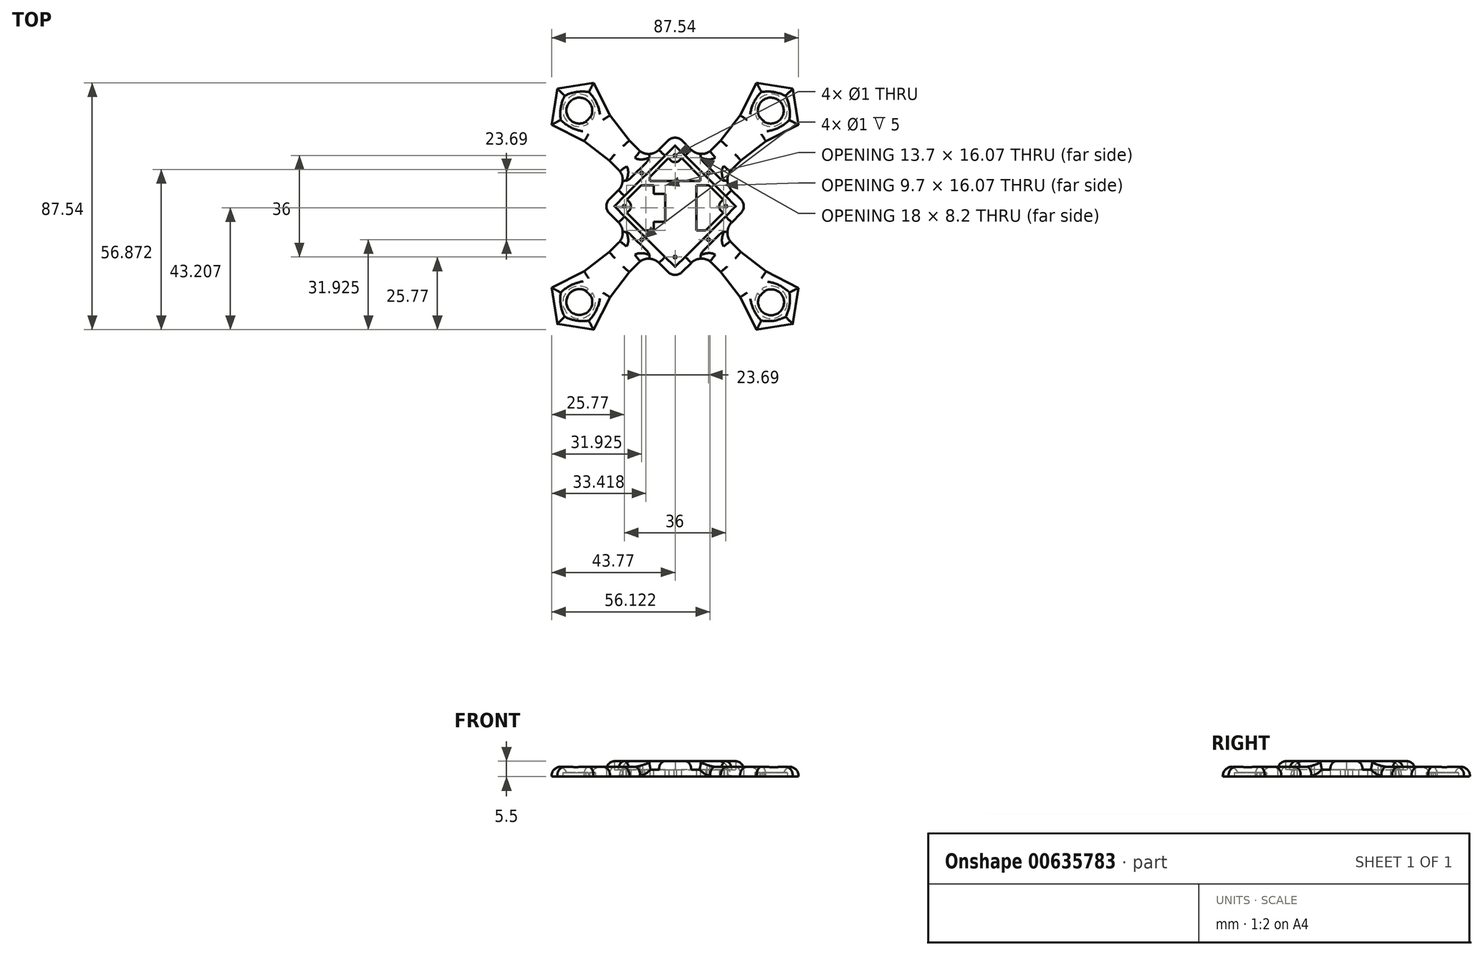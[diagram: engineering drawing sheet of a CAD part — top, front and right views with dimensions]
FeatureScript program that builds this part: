
annotation { "Feature Type Name" : "Feature", "Feature Type Description" : "" }
export const myFeature = defineFeature(function(context is Context, id is Id, definition is map)
    precondition{}
    {
        {
            var Q0;
            Q0=qCreatedBy(makeId("Top.planeOp"),FACE);
            var sketch = newSketch(context, id + "F0", { "sketchPlane" : qUnion([Q0])});
            skCircle(sketch, "E0", {"center": v(0, 18) * mm, "radius": 0.5 * mm});
            skCircle(sketch, "E1.1.0", {"center": v(-18, 0) * mm, "radius": 0.5 * mm});
            skCircle(sketch, "E1.2.0", {"center": v(0, -18) * mm, "radius": 0.5 * mm});
            skCircle(sketch, "E1.3.0", {"center": v(18, 0) * mm, "radius": 0.5 * mm});
            skPoint(sketch, "E1.center", {"position": v(0, 0) * mm});
            skLineSegment(sketch, "E2.0", {"start": v(-9, 10.41) * mm, "end": v(-9, 9) * mm});
            skLineSegment(sketch, "E3.0", {"start": v(9, 10.41) * mm, "end": v(9, 9) * mm});
            skLineSegment(sketch, "E4.0", {"start": v(-9, 9) * mm, "end": v(9, 9) * mm});
            skLineSegment(sketch, "E5.0", {"start": v(-21.54, 0) * mm, "end": v(0, -21.54) * mm});
            skLineSegment(sketch, "E5.1", {"start": v(-21.54, 0) * mm, "end": v(0, 21.54) * mm});
            skLineSegment(sketch, "E5.2", {"start": v(21.54, 0) * mm, "end": v(0, 21.54) * mm});
            skLineSegment(sketch, "E5.3", {"start": v(0, -21.54) * mm, "end": v(21.54, 0) * mm});
            skArc(sketch, "E6.0", {"start": v(-2.21, 17.2) * mm, "mid": v(0, 15.65) * mm, "end": v(2.21, 17.2) * mm});
            skArc(sketch, "E7.1.0", {"start": v(-17.2, -2.21) * mm, "mid": v(-15.65, 0) * mm, "end": v(-17.2, 2.21) * mm});
            skArc(sketch, "E7.3.0", {"start": v(17.2, 2.21) * mm, "mid": v(15.65, 0) * mm, "end": v(17.2, -2.21) * mm});
            skLineSegment(sketch, "E8.0", {"start": v(10.82, -8.6) * mm, "end": v(17.2, -2.21) * mm});
            skLineSegment(sketch, "E8.3", {"start": v(17.2, 2.21) * mm, "end": v(11.94, 7.47) * mm});
            skLineSegment(sketch, "E9.trimOffspring", {"start": v(-9, 10.41) * mm, "end": v(-2.21, 17.2) * mm});
            skLineSegment(sketch, "E10.trimOffspring", {"start": v(9, 10.41) * mm, "end": v(2.21, 17.2) * mm});
            skLineSegment(sketch, "E11.0", {"start": v(7.5, 7.47) * mm, "end": v(7.5, -8.6) * mm});
            skLineSegment(sketch, "E12", {"start": v(11.94, 7.47) * mm, "end": v(7.5, 7.47) * mm});
            skLineSegment(sketch, "E13", {"start": v(7.5, -8.6) * mm, "end": v(10.82, -8.6) * mm});
            skLineSegment(sketch, "E14.MirrorCS", {"start": v(-7.5, -8.6) * mm, "end": v(-10.82, -8.6) * mm});
            skLineSegment(sketch, "E15.MirrorCS", {"start": v(-7.5, 7.47) * mm, "end": v(-7.5, -8.6) * mm});
            skLineSegment(sketch, "E16.MirrorCS", {"start": v(-11.94, 7.47) * mm, "end": v(-7.5, 7.47) * mm});
            skLineSegment(sketch, "E17.MirrorCS", {"start": v(-10.82, -8.6) * mm, "end": v(-17.2, -2.21) * mm});
            skLineSegment(sketch, "E18.MirrorCS", {"start": v(21.54, 0) * mm, "end": v(0, -21.54) * mm});
            skLineSegment(sketch, "E19", {"start": v(-11.94, 7.47) * mm, "end": v(-17.2, 2.21) * mm});
            skSolve(sketch);
        }
        {
            var Q0;
            Q0 = qSketchRegion(id + "F0", true);
            extrude(context, id + "F1", {"entities" : qUnion([Q0]), "depth" : 2.5 * mm, "offsetDistance" : 25 * mm});
        }
        {
            var Q0;
            Q0=makeQuery(id+"F1.opExtrude","CAP_FACE",FACE,{"disambiguationData":[OSD([sQuery(id+"F0.wireOp",EDGE,"E0"),sQuery(id+"F0.wireOp",EDGE,"E1.1.0"),sQuery(id+"F0.wireOp",EDGE,"E1.2.0"),sQuery(id+"F0.wireOp",EDGE,"E1.3.0"),sQuery(id+"F0.wireOp",EDGE,"E2.0"),sQuery(id+"F0.wireOp",EDGE,"E3.0"),sQuery(id+"F0.wireOp",EDGE,"E4.0"),sQuery(id+"F0.wireOp",EDGE,"E5.0"),sQuery(id+"F0.wireOp",EDGE,"E5.1"),sQuery(id+"F0.wireOp",EDGE,"E5.2"),sQuery(id+"F0.wireOp",EDGE,"E6.0"),sQuery(id+"F0.wireOp",EDGE,"E7.1.0"),sQuery(id+"F0.wireOp",EDGE,"E7.3.0"),sQuery(id+"F0.wireOp",EDGE,"E8.0"),sQuery(id+"F0.wireOp",EDGE,"E8.3"),sQuery(id+"F0.wireOp",EDGE,"E9.trimOffspring"),sQuery(id+"F0.wireOp",EDGE,"E10.trimOffspring"),sQuery(id+"F0.wireOp",EDGE,"E11.0"),sQuery(id+"F0.wireOp",EDGE,"E12"),sQuery(id+"F0.wireOp",EDGE,"E13"),sQuery(id+"F0.wireOp",EDGE,"E14.MirrorCS"),sQuery(id+"F0.wireOp",EDGE,"E15.MirrorCS"),sQuery(id+"F0.wireOp",EDGE,"E16.MirrorCS"),sQuery(id+"F0.wireOp",EDGE,"E17.MirrorCS"),sQuery(id+"F0.wireOp",EDGE,"E18.MirrorCS"),sQuery(id+"F0.wireOp",EDGE,"E19")])],"isStart":false});
            var sketch = newSketch(context, id + "F2", { "sketchPlane" : qUnion([Q0])});
            skLineSegment(sketch, "E20", {"start": v(21.54, 0) * mm, "end": v(0, -21.54) * mm});
            skLineSegment(sketch, "E21", {"start": v(0, -21.54) * mm, "end": v(-21.54, 0) * mm});
            skLineSegment(sketch, "E22", {"start": v(-21.54, 0) * mm, "end": v(0, 21.54) * mm});
            skLineSegment(sketch, "E23", {"start": v(0, 21.54) * mm, "end": v(21.54, 0) * mm});
            skLineSegment(sketch, "E24.0", {"start": v(0, -25.78) * mm, "end": v(-25.78, 0) * mm});
            skLineSegment(sketch, "E24.1", {"start": v(25.78, 0) * mm, "end": v(0, -25.78) * mm});
            skLineSegment(sketch, "E24.2", {"start": v(0, 25.78) * mm, "end": v(25.78, 0) * mm});
            skLineSegment(sketch, "E24.3", {"start": v(-25.78, 0) * mm, "end": v(0, 25.78) * mm});
            skSolve(sketch);
        }
        {
            var Q0;
            Q0 = qSketchRegion(id + "F2", true);
            var Q1;
            Q1=makeQuery(id+"F1.opExtrude","CAP_FACE",FACE,{"disambiguationData":[OSD([sQuery(id+"F0.wireOp",EDGE,"E0"),sQuery(id+"F0.wireOp",EDGE,"E1.1.0"),sQuery(id+"F0.wireOp",EDGE,"E1.2.0"),sQuery(id+"F0.wireOp",EDGE,"E1.3.0"),sQuery(id+"F0.wireOp",EDGE,"E2.0"),sQuery(id+"F0.wireOp",EDGE,"E3.0"),sQuery(id+"F0.wireOp",EDGE,"E4.0"),sQuery(id+"F0.wireOp",EDGE,"E5.0"),sQuery(id+"F0.wireOp",EDGE,"E5.1"),sQuery(id+"F0.wireOp",EDGE,"E5.2"),sQuery(id+"F0.wireOp",EDGE,"E6.0"),sQuery(id+"F0.wireOp",EDGE,"E7.1.0"),sQuery(id+"F0.wireOp",EDGE,"E7.3.0"),sQuery(id+"F0.wireOp",EDGE,"E8.0"),sQuery(id+"F0.wireOp",EDGE,"E8.3"),sQuery(id+"F0.wireOp",EDGE,"E9.trimOffspring"),sQuery(id+"F0.wireOp",EDGE,"E10.trimOffspring"),sQuery(id+"F0.wireOp",EDGE,"E11.0"),sQuery(id+"F0.wireOp",EDGE,"E12"),sQuery(id+"F0.wireOp",EDGE,"E13"),sQuery(id+"F0.wireOp",EDGE,"E14.MirrorCS"),sQuery(id+"F0.wireOp",EDGE,"E15.MirrorCS"),sQuery(id+"F0.wireOp",EDGE,"E16.MirrorCS"),sQuery(id+"F0.wireOp",EDGE,"E17.MirrorCS"),sQuery(id+"F0.wireOp",EDGE,"E18.MirrorCS"),sQuery(id+"F0.wireOp",EDGE,"E19")])],"isStart":true});
            extrude(context, id + "F3", {"entities" : qUnion([Q0]), "operationType" : NewBodyOperationType.ADD, "depth" : 3 * mm, "offsetDistance" : 25 * mm, "hasSecondDirection" : true, "secondDirectionBound" : BoundingType.UP_TO_SURFACE, "secondDirectionOppositeDirection" : true, "secondDirectionDepth" : 1.86 * mm, "secondDirectionBoundEntityFace" : qUnion([Q1])});
        }
        {
            var Q0;
            Q0=makeQuery(id+"F1.opExtrude","CAP_FACE",FACE,{"disambiguationData":[OSD([sQuery(id+"F0.wireOp",EDGE,"E0"),sQuery(id+"F0.wireOp",EDGE,"E1.1.0"),sQuery(id+"F0.wireOp",EDGE,"E1.2.0"),sQuery(id+"F0.wireOp",EDGE,"E1.3.0"),sQuery(id+"F0.wireOp",EDGE,"E2.0"),sQuery(id+"F0.wireOp",EDGE,"E3.0"),sQuery(id+"F0.wireOp",EDGE,"E4.0"),sQuery(id+"F0.wireOp",EDGE,"E5.0"),sQuery(id+"F0.wireOp",EDGE,"E5.1"),sQuery(id+"F0.wireOp",EDGE,"E5.2"),sQuery(id+"F0.wireOp",EDGE,"E6.0"),sQuery(id+"F0.wireOp",EDGE,"E7.1.0"),sQuery(id+"F0.wireOp",EDGE,"E7.3.0"),sQuery(id+"F0.wireOp",EDGE,"E8.0"),sQuery(id+"F0.wireOp",EDGE,"E8.3"),sQuery(id+"F0.wireOp",EDGE,"E9.trimOffspring"),sQuery(id+"F0.wireOp",EDGE,"E10.trimOffspring"),sQuery(id+"F0.wireOp",EDGE,"E11.0"),sQuery(id+"F0.wireOp",EDGE,"E12"),sQuery(id+"F0.wireOp",EDGE,"E13"),sQuery(id+"F0.wireOp",EDGE,"E14.MirrorCS"),sQuery(id+"F0.wireOp",EDGE,"E15.MirrorCS"),sQuery(id+"F0.wireOp",EDGE,"E16.MirrorCS"),sQuery(id+"F0.wireOp",EDGE,"E17.MirrorCS"),sQuery(id+"F0.wireOp",EDGE,"E18.MirrorCS"),sQuery(id+"F0.wireOp",EDGE,"E19")])],"isStart":false});
            var sketch = newSketch(context, id + "F4", { "sketchPlane" : qUnion([Q0])});
            skLineSegment(sketch, "E25.0", {"start": v(-3.5, 4.44) * mm, "end": v(-7.5, 4.44) * mm});
            skLineSegment(sketch, "E26.0", {"start": v(-3.5, -5.56) * mm, "end": v(-7.5, -5.56) * mm});
            skLineSegment(sketch, "E27.0", {"start": v(-3.5, -5.56) * mm, "end": v(-3.5, 4.44) * mm});
            skPoint(sketch, "E28.orphan", {"position": v(7.5, -0.56) * mm});
            skPoint(sketch, "E29.end.orphan", {"position": v(-7.5, -0.56) * mm});
            skArc(sketch, "E30", {"start": v(-7.5, 4.44) * mm, "mid": v(-12.5, -0.56) * mm, "end": v(-7.5, -5.56) * mm});
            skSolve(sketch);
        }
        {
            var Q0;
            Q0 = qSketchRegion(id + "F4", true);
            extrude(context, id + "F5", {"entities" : qUnion([Q0]), "operationType" : NewBodyOperationType.REMOVE, "oppositeDirection" : true, "depth" : 25 * mm, "offsetDistance" : 25 * mm});
        }
        {
            var Q0;
            Q0=makeQuery(id+"F3.opExtrude","SWEPT_EDGE",EDGE,{"disambiguationData":[OSD([sQuery(id+"F2.wireOp",EDGE,"E24.2"),sQuery(id+"F2.wireOp",EDGE,"E24.3")])]});
            var Q1;
            Q1=makeQuery(id+"F3.opExtrude","SWEPT_EDGE",EDGE,{"disambiguationData":[OSD([sQuery(id+"F2.wireOp",EDGE,"E24.1"),sQuery(id+"F2.wireOp",EDGE,"E24.2")])]});
            var Q2;
            Q2=makeQuery(id+"F3.opExtrude","SWEPT_EDGE",EDGE,{"disambiguationData":[OSD([sQuery(id+"F2.wireOp",EDGE,"E24.0"),sQuery(id+"F2.wireOp",EDGE,"E24.1")])]});
            var Q3;
            Q3=makeQuery(id+"F3.opExtrude","SWEPT_EDGE",EDGE,{"disambiguationData":[OSD([sQuery(id+"F2.wireOp",EDGE,"E24.0"),sQuery(id+"F2.wireOp",EDGE,"E24.3")])]});
            fillet(context, id + "F6", {"entities" : qUnion([Q0, Q1, Q2, Q3]), "radius" : 3.5 * mm, "tangentPropagation" : true, "allowEdgeOverflow" : false});
        }
        {
            var Q0;
            {var subQ0=sQuery(id+"F0.wireOp",EDGE,"E19");var subQ1=sQuery(id+"F0.wireOp",EDGE,"E18.MirrorCS");var subQ2=sQuery(id+"F0.wireOp",EDGE,"E17.MirrorCS");var subQ3=sQuery(id+"F0.wireOp",EDGE,"E16.MirrorCS");var subQ4=sQuery(id+"F0.wireOp",EDGE,"E15.MirrorCS");var subQ5=sQuery(id+"F0.wireOp",EDGE,"E14.MirrorCS");var subQ6=sQuery(id+"F0.wireOp",EDGE,"E13");var subQ7=sQuery(id+"F0.wireOp",EDGE,"E12");var subQ8=sQuery(id+"F0.wireOp",EDGE,"E11.0");var subQ9=sQuery(id+"F0.wireOp",EDGE,"E10.trimOffspring");var subQ10=sQuery(id+"F0.wireOp",EDGE,"E9.trimOffspring");var subQ11=sQuery(id+"F0.wireOp",EDGE,"E8.3");var subQ12=sQuery(id+"F0.wireOp",EDGE,"E8.0");var subQ13=sQuery(id+"F0.wireOp",EDGE,"E7.3.0");var subQ14=sQuery(id+"F0.wireOp",EDGE,"E7.1.0");var subQ15=sQuery(id+"F0.wireOp",EDGE,"E6.0");var subQ16=sQuery(id+"F0.wireOp",EDGE,"E5.2");var subQ17=sQuery(id+"F0.wireOp",EDGE,"E5.1");var subQ18=sQuery(id+"F0.wireOp",EDGE,"E5.0");var subQ19=sQuery(id+"F0.wireOp",EDGE,"E4.0");var subQ20=sQuery(id+"F0.wireOp",EDGE,"E3.0");var subQ21=sQuery(id+"F0.wireOp",EDGE,"E2.0");var subQ22=sQuery(id+"F0.wireOp",EDGE,"E1.3.0");var subQ23=sQuery(id+"F0.wireOp",EDGE,"E1.2.0");var subQ24=sQuery(id+"F0.wireOp",EDGE,"E1.1.0");var subQ25=sQuery(id+"F0.wireOp",EDGE,"E0");Q0=makeQuery(id+"F3.boolean.opBoolean","MERGE",FACE,{"derivedFrom":[makeQuery(id+"F1.opExtrude","CAP_FACE",FACE,{"disambiguationData":[OSD([subQ25,subQ24,subQ23,subQ22,subQ21,subQ20,subQ19,subQ18,subQ17,subQ16,subQ15,subQ14,subQ13,subQ12,subQ11,subQ10,subQ9,subQ8,subQ7,subQ6,subQ5,subQ4,subQ3,subQ2,subQ1,subQ0])],"isStart":true}),makeQuery(id+"F3.opExtrude","CAP_FACE",FACE,{"disambiguationData":[OSD([subQ25,subQ24,subQ23,subQ22,subQ21,subQ20,subQ19,subQ18,subQ17,subQ16,subQ15,subQ14,subQ13,subQ12,subQ11,subQ10,subQ9,subQ8,subQ7,subQ6,subQ5,subQ4,subQ3,subQ2,subQ1,subQ0])],"isStart":true})]});}
            var sketch = newSketch(context, id + "F7", { "sketchPlane" : qUnion([Q0])});
            skCircle(sketch, "E31", {"center": v(34.04, 34.04) * mm, "radius": 4.45 * mm});
            skCircle(sketch, "E32.1.0", {"center": v(-33.94, 33.94) * mm, "radius": 4.45 * mm});
            skCircle(sketch, "E32.2.0", {"center": v(-33.94, -33.94) * mm, "radius": 4.45 * mm});
            skCircle(sketch, "E32.3.0", {"center": v(33.94, -33.94) * mm, "radius": 4.45 * mm});
            skLineSegment(sketch, "E33", {"start": v(-15.4, -8.31) * mm, "end": v(-8.33, -15.38) * mm});
            skLineSegment(sketch, "E34.0", {"start": v(-15.4, -8.31) * mm, "end": v(-23.3, -16.2) * mm});
            skLineSegment(sketch, "E35.0", {"start": v(-8.33, -15.38) * mm, "end": v(-16.23, -23.28) * mm});
            skLineSegment(sketch, "E36.1", {"start": v(-23.08, -32.2) * mm, "end": v(-28.93, -43.73) * mm});
            skLineSegment(sketch, "E36.2", {"start": v(-28.93, -43.73) * mm, "end": v(-41.7, -41.73) * mm});
            skLineSegment(sketch, "E36.3", {"start": v(-41.7, -41.73) * mm, "end": v(-43.75, -28.97) * mm});
            skLineSegment(sketch, "E36.4", {"start": v(-43.75, -28.97) * mm, "end": v(-32.24, -23.08) * mm});
            skPoint(sketch, "E36.0.midPoint", {"position": v(-27.66, -27.64) * mm});
            skPoint(sketch, "E37.start.orphan", {"position": v(-11.87, -11.85) * mm});
            skLineSegment(sketch, "E38", {"start": v(-32.24, -23.08) * mm, "end": v(-23.3, -16.2) * mm});
            skLineSegment(sketch, "E39", {"start": v(-23.08, -32.2) * mm, "end": v(-16.23, -23.28) * mm});
            skPoint(sketch, "E40.orphan", {"position": v(-24.13, -31.18) * mm});
            skPoint(sketch, "E41.orphan", {"position": v(-31.2, -24.1) * mm});
            skLineSegment(sketch, "E42.1.0", {"start": v(32.2, -23.08) * mm, "end": v(23.28, -16.23) * mm});
            skLineSegment(sketch, "E42.1.1", {"start": v(8.31, -15.4) * mm, "end": v(15.38, -8.33) * mm});
            skLineSegment(sketch, "E42.1.2", {"start": v(23.08, -32.24) * mm, "end": v(16.2, -23.3) * mm});
            skLineSegment(sketch, "E42.1.3", {"start": v(8.31, -15.4) * mm, "end": v(16.2, -23.3) * mm});
            skLineSegment(sketch, "E42.1.4", {"start": v(28.97, -43.75) * mm, "end": v(23.08, -32.24) * mm});
            skLineSegment(sketch, "E42.1.5", {"start": v(41.73, -41.7) * mm, "end": v(28.97, -43.75) * mm});
            skLineSegment(sketch, "E42.1.6", {"start": v(15.38, -8.33) * mm, "end": v(23.28, -16.23) * mm});
            skLineSegment(sketch, "E42.1.7", {"start": v(43.73, -28.93) * mm, "end": v(41.73, -41.7) * mm});
            skLineSegment(sketch, "E42.1.8", {"start": v(32.2, -23.08) * mm, "end": v(43.73, -28.93) * mm});
            skLineSegment(sketch, "E42.2.0", {"start": v(23.08, 32.2) * mm, "end": v(16.23, 23.28) * mm});
            skLineSegment(sketch, "E42.2.1", {"start": v(15.4, 8.31) * mm, "end": v(8.33, 15.38) * mm});
            skLineSegment(sketch, "E42.2.2", {"start": v(32.24, 23.08) * mm, "end": v(23.3, 16.2) * mm});
            skLineSegment(sketch, "E42.2.3", {"start": v(15.4, 8.31) * mm, "end": v(23.3, 16.2) * mm});
            skLineSegment(sketch, "E42.2.4", {"start": v(43.75, 28.97) * mm, "end": v(32.24, 23.08) * mm});
            skLineSegment(sketch, "E42.2.5", {"start": v(41.7, 41.73) * mm, "end": v(43.75, 28.97) * mm});
            skLineSegment(sketch, "E42.2.6", {"start": v(8.33, 15.38) * mm, "end": v(16.23, 23.28) * mm});
            skLineSegment(sketch, "E42.2.7", {"start": v(28.93, 43.73) * mm, "end": v(41.7, 41.73) * mm});
            skLineSegment(sketch, "E42.2.8", {"start": v(23.08, 32.2) * mm, "end": v(28.93, 43.73) * mm});
            skLineSegment(sketch, "E42.3.0", {"start": v(-32.2, 23.08) * mm, "end": v(-23.28, 16.23) * mm});
            skLineSegment(sketch, "E42.3.1", {"start": v(-8.31, 15.4) * mm, "end": v(-15.38, 8.33) * mm});
            skLineSegment(sketch, "E42.3.2", {"start": v(-23.08, 32.24) * mm, "end": v(-16.2, 23.3) * mm});
            skLineSegment(sketch, "E42.3.3", {"start": v(-8.31, 15.4) * mm, "end": v(-16.2, 23.3) * mm});
            skLineSegment(sketch, "E42.3.4", {"start": v(-28.97, 43.75) * mm, "end": v(-23.08, 32.24) * mm});
            skLineSegment(sketch, "E42.3.5", {"start": v(-41.73, 41.7) * mm, "end": v(-28.97, 43.75) * mm});
            skLineSegment(sketch, "E42.3.6", {"start": v(-15.38, 8.33) * mm, "end": v(-23.28, 16.23) * mm});
            skLineSegment(sketch, "E42.3.7", {"start": v(-43.73, 28.93) * mm, "end": v(-41.73, 41.7) * mm});
            skLineSegment(sketch, "E42.3.8", {"start": v(-32.2, 23.08) * mm, "end": v(-43.73, 28.93) * mm});
            skSolve(sketch);
        }
        {
            var Q0;
            Q0 = qSketchRegion(id + "F7", true);
            extrude(context, id + "F8", {"entities" : qUnion([Q0]), "operationType" : NewBodyOperationType.ADD, "oppositeDirection" : true, "depth" : 3.5 * mm, "offsetDistance" : 25 * mm, "hasDraft" : true, "draftAngle" : 3 * degree});
        }
        {
            var Q0;
            Q0=makeQuery(id+"F8.boolean.opBoolean","INTERSECT",EDGE,{"derivedFrom":[makeQuery(id+"F3.opExtrude","SWEPT_FACE",FACE,{"disambiguationData":[OSD([sQuery(id+"F2.wireOp",EDGE,"E24.2")])]}),makeQuery(id+"F8.opExtrude","CAP_FACE",FACE,{"disambiguationData":[OSD([sQuery(id+"F7.wireOp",EDGE,"E32.3.0"),sQuery(id+"F7.wireOp",EDGE,"E42.1.0"),sQuery(id+"F7.wireOp",EDGE,"E42.1.1"),sQuery(id+"F7.wireOp",EDGE,"E42.1.2"),sQuery(id+"F7.wireOp",EDGE,"E42.1.3"),sQuery(id+"F7.wireOp",EDGE,"E42.1.4"),sQuery(id+"F7.wireOp",EDGE,"E42.1.5"),sQuery(id+"F7.wireOp",EDGE,"E42.1.6"),sQuery(id+"F7.wireOp",EDGE,"E42.1.7"),sQuery(id+"F7.wireOp",EDGE,"E42.1.8")])],"isStart":false})]});
            var Q1;
            Q1=makeQuery(id+"F8.boolean.opBoolean","INTERSECT",EDGE,{"derivedFrom":[makeQuery(id+"F3.opExtrude","SWEPT_FACE",FACE,{"disambiguationData":[OSD([sQuery(id+"F2.wireOp",EDGE,"E24.2")])]}),makeQuery(id+"F8.opExtrude","SWEPT_FACE",FACE,{"disambiguationData":[OSD([sQuery(id+"F7.wireOp",EDGE,"E42.1.3")])]})]});
            var Q2;
            Q2=makeQuery(id+"F8.boolean.opBoolean","INTERSECT",EDGE,{"derivedFrom":[makeQuery(id+"F3.opExtrude","SWEPT_FACE",FACE,{"disambiguationData":[OSD([sQuery(id+"F2.wireOp",EDGE,"E24.2")])]}),makeQuery(id+"F8.opExtrude","SWEPT_FACE",FACE,{"disambiguationData":[OSD([sQuery(id+"F7.wireOp",EDGE,"E42.1.6")])]})]});
            var Q3;
            Q3=makeQuery(id+"F8.boolean.opBoolean","INTERSECT",EDGE,{"derivedFrom":[makeQuery(id+"F3.opExtrude","SWEPT_FACE",FACE,{"disambiguationData":[OSD([sQuery(id+"F2.wireOp",EDGE,"E24.3")])]}),makeQuery(id+"F8.opExtrude","CAP_FACE",FACE,{"disambiguationData":[OSD([sQuery(id+"F7.wireOp",EDGE,"E32.2.0"),sQuery(id+"F7.wireOp",EDGE,"E33"),sQuery(id+"F7.wireOp",EDGE,"E34.0"),sQuery(id+"F7.wireOp",EDGE,"E35.0"),sQuery(id+"F7.wireOp",EDGE,"E36.1"),sQuery(id+"F7.wireOp",EDGE,"E36.2"),sQuery(id+"F7.wireOp",EDGE,"E36.3"),sQuery(id+"F7.wireOp",EDGE,"E36.4"),sQuery(id+"F7.wireOp",EDGE,"E38"),sQuery(id+"F7.wireOp",EDGE,"E39")])],"isStart":false})]});
            var Q4;
            Q4=makeQuery(id+"F8.boolean.opBoolean","INTERSECT",EDGE,{"derivedFrom":[makeQuery(id+"F3.opExtrude","SWEPT_FACE",FACE,{"disambiguationData":[OSD([sQuery(id+"F2.wireOp",EDGE,"E24.3")])]}),makeQuery(id+"F8.opExtrude","SWEPT_FACE",FACE,{"disambiguationData":[OSD([sQuery(id+"F7.wireOp",EDGE,"E35.0")])]})]});
            var Q5;
            Q5=makeQuery(id+"F8.boolean.opBoolean","INTERSECT",EDGE,{"derivedFrom":[makeQuery(id+"F3.opExtrude","SWEPT_FACE",FACE,{"disambiguationData":[OSD([sQuery(id+"F2.wireOp",EDGE,"E24.3")])]}),makeQuery(id+"F8.opExtrude","SWEPT_FACE",FACE,{"disambiguationData":[OSD([sQuery(id+"F7.wireOp",EDGE,"E34.0")])]})]});
            var Q6;
            Q6=makeQuery(id+"F8.boolean.opBoolean","INTERSECT",EDGE,{"derivedFrom":[makeQuery(id+"F3.opExtrude","SWEPT_FACE",FACE,{"disambiguationData":[OSD([sQuery(id+"F2.wireOp",EDGE,"E24.0")])]}),makeQuery(id+"F8.opExtrude","SWEPT_FACE",FACE,{"disambiguationData":[OSD([sQuery(id+"F7.wireOp",EDGE,"E42.3.6")])]})]});
            var Q7;
            Q7=makeQuery(id+"F8.boolean.opBoolean","INTERSECT",EDGE,{"derivedFrom":[makeQuery(id+"F3.opExtrude","SWEPT_FACE",FACE,{"disambiguationData":[OSD([sQuery(id+"F2.wireOp",EDGE,"E24.0")])]}),makeQuery(id+"F8.opExtrude","CAP_FACE",FACE,{"disambiguationData":[OSD([sQuery(id+"F7.wireOp",EDGE,"E32.1.0"),sQuery(id+"F7.wireOp",EDGE,"E42.3.0"),sQuery(id+"F7.wireOp",EDGE,"E42.3.1"),sQuery(id+"F7.wireOp",EDGE,"E42.3.2"),sQuery(id+"F7.wireOp",EDGE,"E42.3.3"),sQuery(id+"F7.wireOp",EDGE,"E42.3.4"),sQuery(id+"F7.wireOp",EDGE,"E42.3.5"),sQuery(id+"F7.wireOp",EDGE,"E42.3.6"),sQuery(id+"F7.wireOp",EDGE,"E42.3.7"),sQuery(id+"F7.wireOp",EDGE,"E42.3.8")])],"isStart":false})]});
            var Q8;
            Q8=makeQuery(id+"F8.boolean.opBoolean","INTERSECT",EDGE,{"derivedFrom":[makeQuery(id+"F3.opExtrude","SWEPT_FACE",FACE,{"disambiguationData":[OSD([sQuery(id+"F2.wireOp",EDGE,"E24.0")])]}),makeQuery(id+"F8.opExtrude","SWEPT_FACE",FACE,{"disambiguationData":[OSD([sQuery(id+"F7.wireOp",EDGE,"E42.3.3")])]})]});
            var Q9;
            Q9=makeQuery(id+"F8.boolean.opBoolean","INTERSECT",EDGE,{"derivedFrom":[makeQuery(id+"F3.opExtrude","SWEPT_FACE",FACE,{"disambiguationData":[OSD([sQuery(id+"F2.wireOp",EDGE,"E24.1")])]}),makeQuery(id+"F8.opExtrude","SWEPT_FACE",FACE,{"disambiguationData":[OSD([sQuery(id+"F7.wireOp",EDGE,"E42.2.6")])]})]});
            var Q10;
            Q10=makeQuery(id+"F8.boolean.opBoolean","INTERSECT",EDGE,{"derivedFrom":[makeQuery(id+"F3.opExtrude","SWEPT_FACE",FACE,{"disambiguationData":[OSD([sQuery(id+"F2.wireOp",EDGE,"E24.1")])]}),makeQuery(id+"F8.opExtrude","CAP_FACE",FACE,{"disambiguationData":[OSD([sQuery(id+"F7.wireOp",EDGE,"E31"),sQuery(id+"F7.wireOp",EDGE,"E42.2.0"),sQuery(id+"F7.wireOp",EDGE,"E42.2.1"),sQuery(id+"F7.wireOp",EDGE,"E42.2.2"),sQuery(id+"F7.wireOp",EDGE,"E42.2.3"),sQuery(id+"F7.wireOp",EDGE,"E42.2.4"),sQuery(id+"F7.wireOp",EDGE,"E42.2.5"),sQuery(id+"F7.wireOp",EDGE,"E42.2.6"),sQuery(id+"F7.wireOp",EDGE,"E42.2.7"),sQuery(id+"F7.wireOp",EDGE,"E42.2.8")])],"isStart":false})]});
            var Q11;
            Q11=makeQuery(id+"F8.boolean.opBoolean","INTERSECT",EDGE,{"derivedFrom":[makeQuery(id+"F3.opExtrude","SWEPT_FACE",FACE,{"disambiguationData":[OSD([sQuery(id+"F2.wireOp",EDGE,"E24.1")])]}),makeQuery(id+"F8.opExtrude","SWEPT_FACE",FACE,{"disambiguationData":[OSD([sQuery(id+"F7.wireOp",EDGE,"E42.2.3")])]})]});
            fillet(context, id + "F9", {"entities" : qUnion([Q0, Q1, Q2, Q3, Q4, Q5, Q6, Q7, Q8, Q9, Q10, Q11]), "radius" : 5 * mm, "tangentPropagation" : true, "allowEdgeOverflow" : false});
        }
        {
            var Q0;
            Q0=makeQuery(id+"F8.opExtrude","CAP_FACE",FACE,{"disambiguationData":[OSD([sQuery(id+"F7.wireOp",EDGE,"E32.1.0"),sQuery(id+"F7.wireOp",EDGE,"E42.3.0"),sQuery(id+"F7.wireOp",EDGE,"E42.3.1"),sQuery(id+"F7.wireOp",EDGE,"E42.3.2"),sQuery(id+"F7.wireOp",EDGE,"E42.3.3"),sQuery(id+"F7.wireOp",EDGE,"E42.3.4"),sQuery(id+"F7.wireOp",EDGE,"E42.3.5"),sQuery(id+"F7.wireOp",EDGE,"E42.3.6"),sQuery(id+"F7.wireOp",EDGE,"E42.3.7"),sQuery(id+"F7.wireOp",EDGE,"E42.3.8")])],"isStart":false});
            var Q1;
            Q1=makeQuery(id+"F8.opExtrude","CAP_FACE",FACE,{"disambiguationData":[OSD([sQuery(id+"F7.wireOp",EDGE,"E31"),sQuery(id+"F7.wireOp",EDGE,"E42.2.0"),sQuery(id+"F7.wireOp",EDGE,"E42.2.1"),sQuery(id+"F7.wireOp",EDGE,"E42.2.2"),sQuery(id+"F7.wireOp",EDGE,"E42.2.3"),sQuery(id+"F7.wireOp",EDGE,"E42.2.4"),sQuery(id+"F7.wireOp",EDGE,"E42.2.5"),sQuery(id+"F7.wireOp",EDGE,"E42.2.6"),sQuery(id+"F7.wireOp",EDGE,"E42.2.7"),sQuery(id+"F7.wireOp",EDGE,"E42.2.8")])],"isStart":false});
            var Q2;
            Q2=makeQuery(id+"F8.opExtrude","CAP_FACE",FACE,{"disambiguationData":[OSD([sQuery(id+"F7.wireOp",EDGE,"E32.3.0"),sQuery(id+"F7.wireOp",EDGE,"E42.1.0"),sQuery(id+"F7.wireOp",EDGE,"E42.1.1"),sQuery(id+"F7.wireOp",EDGE,"E42.1.2"),sQuery(id+"F7.wireOp",EDGE,"E42.1.3"),sQuery(id+"F7.wireOp",EDGE,"E42.1.4"),sQuery(id+"F7.wireOp",EDGE,"E42.1.5"),sQuery(id+"F7.wireOp",EDGE,"E42.1.6"),sQuery(id+"F7.wireOp",EDGE,"E42.1.7"),sQuery(id+"F7.wireOp",EDGE,"E42.1.8")])],"isStart":false});
            var Q3;
            Q3=makeQuery(id+"F8.opExtrude","CAP_FACE",FACE,{"disambiguationData":[OSD([sQuery(id+"F7.wireOp",EDGE,"E32.2.0"),sQuery(id+"F7.wireOp",EDGE,"E33"),sQuery(id+"F7.wireOp",EDGE,"E34.0"),sQuery(id+"F7.wireOp",EDGE,"E35.0"),sQuery(id+"F7.wireOp",EDGE,"E36.1"),sQuery(id+"F7.wireOp",EDGE,"E36.2"),sQuery(id+"F7.wireOp",EDGE,"E36.3"),sQuery(id+"F7.wireOp",EDGE,"E36.4"),sQuery(id+"F7.wireOp",EDGE,"E38"),sQuery(id+"F7.wireOp",EDGE,"E39")])],"isStart":false});
            fillet(context, id + "F10", {"entities" : qUnion([Q0, Q1, Q2, Q3]), "radius" : 3 * mm, "tangentPropagation" : true, "allowEdgeOverflow" : false});
        }
        {
            var Q0;
            {var subQ0=sQuery(id+"F0.wireOp",EDGE,"E19");var subQ1=sQuery(id+"F0.wireOp",EDGE,"E18.MirrorCS");var subQ2=sQuery(id+"F0.wireOp",EDGE,"E17.MirrorCS");var subQ3=sQuery(id+"F0.wireOp",EDGE,"E16.MirrorCS");var subQ4=sQuery(id+"F0.wireOp",EDGE,"E15.MirrorCS");var subQ5=sQuery(id+"F0.wireOp",EDGE,"E14.MirrorCS");var subQ6=sQuery(id+"F0.wireOp",EDGE,"E13");var subQ7=sQuery(id+"F0.wireOp",EDGE,"E12");var subQ8=sQuery(id+"F0.wireOp",EDGE,"E11.0");var subQ9=sQuery(id+"F0.wireOp",EDGE,"E10.trimOffspring");var subQ10=sQuery(id+"F0.wireOp",EDGE,"E9.trimOffspring");var subQ11=sQuery(id+"F0.wireOp",EDGE,"E8.3");var subQ12=sQuery(id+"F0.wireOp",EDGE,"E8.0");var subQ13=sQuery(id+"F0.wireOp",EDGE,"E7.3.0");var subQ14=sQuery(id+"F0.wireOp",EDGE,"E7.1.0");var subQ15=sQuery(id+"F0.wireOp",EDGE,"E6.0");var subQ16=sQuery(id+"F0.wireOp",EDGE,"E5.2");var subQ17=sQuery(id+"F0.wireOp",EDGE,"E5.1");var subQ18=sQuery(id+"F0.wireOp",EDGE,"E5.0");var subQ19=sQuery(id+"F0.wireOp",EDGE,"E4.0");var subQ20=sQuery(id+"F0.wireOp",EDGE,"E3.0");var subQ21=sQuery(id+"F0.wireOp",EDGE,"E2.0");var subQ22=sQuery(id+"F0.wireOp",EDGE,"E1.3.0");var subQ23=sQuery(id+"F0.wireOp",EDGE,"E1.2.0");var subQ24=sQuery(id+"F0.wireOp",EDGE,"E1.1.0");var subQ25=sQuery(id+"F0.wireOp",EDGE,"E0");Q0=makeQuery(id+"F8.boolean.opBoolean","MERGE",FACE,{"derivedFrom":[makeQuery(id+"F3.boolean.opBoolean","MERGE",FACE,{"derivedFrom":[makeQuery(id+"F1.opExtrude","CAP_FACE",FACE,{"disambiguationData":[OSD([subQ25,subQ24,subQ23,subQ22,subQ21,subQ20,subQ19,subQ18,subQ17,subQ16,subQ15,subQ14,subQ13,subQ12,subQ11,subQ10,subQ9,subQ8,subQ7,subQ6,subQ5,subQ4,subQ3,subQ2,subQ1,subQ0])],"isStart":true}),makeQuery(id+"F3.opExtrude","CAP_FACE",FACE,{"disambiguationData":[OSD([subQ25,subQ24,subQ23,subQ22,subQ21,subQ20,subQ19,subQ18,subQ17,subQ16,subQ15,subQ14,subQ13,subQ12,subQ11,subQ10,subQ9,subQ8,subQ7,subQ6,subQ5,subQ4,subQ3,subQ2,subQ1,subQ0])],"isStart":true})]}),makeQuery(id+"F8.opExtrude","CAP_FACE",FACE,{"disambiguationData":[OSD([sQuery(id+"F7.wireOp",EDGE,"E31"),sQuery(id+"F7.wireOp",EDGE,"E42.2.0"),sQuery(id+"F7.wireOp",EDGE,"E42.2.1"),sQuery(id+"F7.wireOp",EDGE,"E42.2.2"),sQuery(id+"F7.wireOp",EDGE,"E42.2.3"),sQuery(id+"F7.wireOp",EDGE,"E42.2.4"),sQuery(id+"F7.wireOp",EDGE,"E42.2.5"),sQuery(id+"F7.wireOp",EDGE,"E42.2.6"),sQuery(id+"F7.wireOp",EDGE,"E42.2.7"),sQuery(id+"F7.wireOp",EDGE,"E42.2.8")])],"isStart":true}),makeQuery(id+"F8.opExtrude","CAP_FACE",FACE,{"disambiguationData":[OSD([sQuery(id+"F7.wireOp",EDGE,"E32.1.0"),sQuery(id+"F7.wireOp",EDGE,"E42.3.0"),sQuery(id+"F7.wireOp",EDGE,"E42.3.1"),sQuery(id+"F7.wireOp",EDGE,"E42.3.2"),sQuery(id+"F7.wireOp",EDGE,"E42.3.3"),sQuery(id+"F7.wireOp",EDGE,"E42.3.4"),sQuery(id+"F7.wireOp",EDGE,"E42.3.5"),sQuery(id+"F7.wireOp",EDGE,"E42.3.6"),sQuery(id+"F7.wireOp",EDGE,"E42.3.7"),sQuery(id+"F7.wireOp",EDGE,"E42.3.8")])],"isStart":true}),makeQuery(id+"F8.opExtrude","CAP_FACE",FACE,{"disambiguationData":[OSD([sQuery(id+"F7.wireOp",EDGE,"E32.2.0"),sQuery(id+"F7.wireOp",EDGE,"E33"),sQuery(id+"F7.wireOp",EDGE,"E34.0"),sQuery(id+"F7.wireOp",EDGE,"E35.0"),sQuery(id+"F7.wireOp",EDGE,"E36.1"),sQuery(id+"F7.wireOp",EDGE,"E36.2"),sQuery(id+"F7.wireOp",EDGE,"E36.3"),sQuery(id+"F7.wireOp",EDGE,"E36.4"),sQuery(id+"F7.wireOp",EDGE,"E38"),sQuery(id+"F7.wireOp",EDGE,"E39")])],"isStart":true}),makeQuery(id+"F8.opExtrude","CAP_FACE",FACE,{"disambiguationData":[OSD([sQuery(id+"F7.wireOp",EDGE,"E32.3.0"),sQuery(id+"F7.wireOp",EDGE,"E42.1.0"),sQuery(id+"F7.wireOp",EDGE,"E42.1.1"),sQuery(id+"F7.wireOp",EDGE,"E42.1.2"),sQuery(id+"F7.wireOp",EDGE,"E42.1.3"),sQuery(id+"F7.wireOp",EDGE,"E42.1.4"),sQuery(id+"F7.wireOp",EDGE,"E42.1.5"),sQuery(id+"F7.wireOp",EDGE,"E42.1.6"),sQuery(id+"F7.wireOp",EDGE,"E42.1.7"),sQuery(id+"F7.wireOp",EDGE,"E42.1.8")])],"isStart":true})]});}
            var sketch = newSketch(context, id + "F11", { "sketchPlane" : qUnion([Q0])});
            skArc(sketch, "E43", {"start": v(30.75, 29.33) * mm, "mid": v(38.11, 38.11) * mm, "end": v(29.33, 30.75) * mm});
            skLineSegment(sketch, "E44", {"start": v(32.59, 34) * mm, "end": v(34.05, 32.54) * mm});
            skLineSegment(sketch, "E45", {"start": v(29.33, 30.75) * mm, "end": v(32.59, 34) * mm});
            skLineSegment(sketch, "E46", {"start": v(30.75, 29.33) * mm, "end": v(34.05, 32.54) * mm});
            skArc(sketch, "E47.1.0", {"start": v(-29.33, 30.75) * mm, "mid": v(-38.11, 38.11) * mm, "end": v(-30.75, 29.33) * mm});
            skLineSegment(sketch, "E47.1.1", {"start": v(-34, 32.59) * mm, "end": v(-32.54, 34.05) * mm});
            skLineSegment(sketch, "E47.1.2", {"start": v(-30.75, 29.33) * mm, "end": v(-34, 32.59) * mm});
            skLineSegment(sketch, "E47.1.3", {"start": v(-29.33, 30.75) * mm, "end": v(-32.54, 34.05) * mm});
            skArc(sketch, "E47.2.0", {"start": v(-30.75, -29.33) * mm, "mid": v(-38.11, -38.11) * mm, "end": v(-29.33, -30.75) * mm});
            skLineSegment(sketch, "E47.2.1", {"start": v(-32.59, -34) * mm, "end": v(-34.05, -32.54) * mm});
            skLineSegment(sketch, "E47.2.2", {"start": v(-29.33, -30.75) * mm, "end": v(-32.59, -34) * mm});
            skLineSegment(sketch, "E47.2.3", {"start": v(-30.75, -29.33) * mm, "end": v(-34.05, -32.54) * mm});
            skArc(sketch, "E47.3.0", {"start": v(29.33, -30.75) * mm, "mid": v(38.11, -38.11) * mm, "end": v(30.75, -29.33) * mm});
            skLineSegment(sketch, "E47.3.1", {"start": v(34, -32.59) * mm, "end": v(32.54, -34.05) * mm});
            skLineSegment(sketch, "E47.3.2", {"start": v(30.75, -29.33) * mm, "end": v(34, -32.59) * mm});
            skLineSegment(sketch, "E47.3.3", {"start": v(29.33, -30.75) * mm, "end": v(32.54, -34.05) * mm});
            skPoint(sketch, "E47.center", {"position": v(0, 0) * mm});
            skSolve(sketch);
        }
        {
            var Q0;
            Q0 = qSketchRegion(id + "F11", true);
            extrude(context, id + "F12", {"entities" : qUnion([Q0]), "operationType" : NewBodyOperationType.REMOVE, "oppositeDirection" : true, "depth" : 1.5 * mm, "offsetDistance" : 25 * mm});
        }
        {
            var Q0;
            Q0=makeQuery(id+"F3.opExtrude","CAP_FACE",FACE,{"disambiguationData":[OSD([sQuery(id+"F2.wireOp",EDGE,"E20"),sQuery(id+"F2.wireOp",EDGE,"E21"),sQuery(id+"F2.wireOp",EDGE,"E22"),sQuery(id+"F2.wireOp",EDGE,"E23"),sQuery(id+"F2.wireOp",EDGE,"E24.0"),sQuery(id+"F2.wireOp",EDGE,"E24.1"),sQuery(id+"F2.wireOp",EDGE,"E24.2"),sQuery(id+"F2.wireOp",EDGE,"E24.3")])],"isStart":false});
            var sketch = newSketch(context, id + "F13", { "sketchPlane" : qUnion([Q0])});
            skPoint(sketch, "E48.endSnap0", {"position": v(10.77, -10.77) * mm});
            skCircle(sketch, "E49", {"center": v(11.84, -11.82) * mm, "radius": 0.5 * mm});
            skCircle(sketch, "E50.1.0", {"center": v(11.82, 11.84) * mm, "radius": 0.5 * mm});
            skCircle(sketch, "E50.2.0", {"center": v(-11.84, 11.82) * mm, "radius": 0.5 * mm});
            skCircle(sketch, "E50.3.0", {"center": v(-11.82, -11.84) * mm, "radius": 0.5 * mm});
            skPoint(sketch, "E50.center", {"position": v(0, 0) * mm});
            skSolve(sketch);
        }
        {
            var Q0;
            Q0 = qSketchRegion(id + "F13", true);
            extrude(context, id + "F14", {"entities" : qUnion([Q0]), "operationType" : NewBodyOperationType.REMOVE, "oppositeDirection" : true, "depth" : 5 * mm, "offsetDistance" : 25 * mm});
        }
    });
